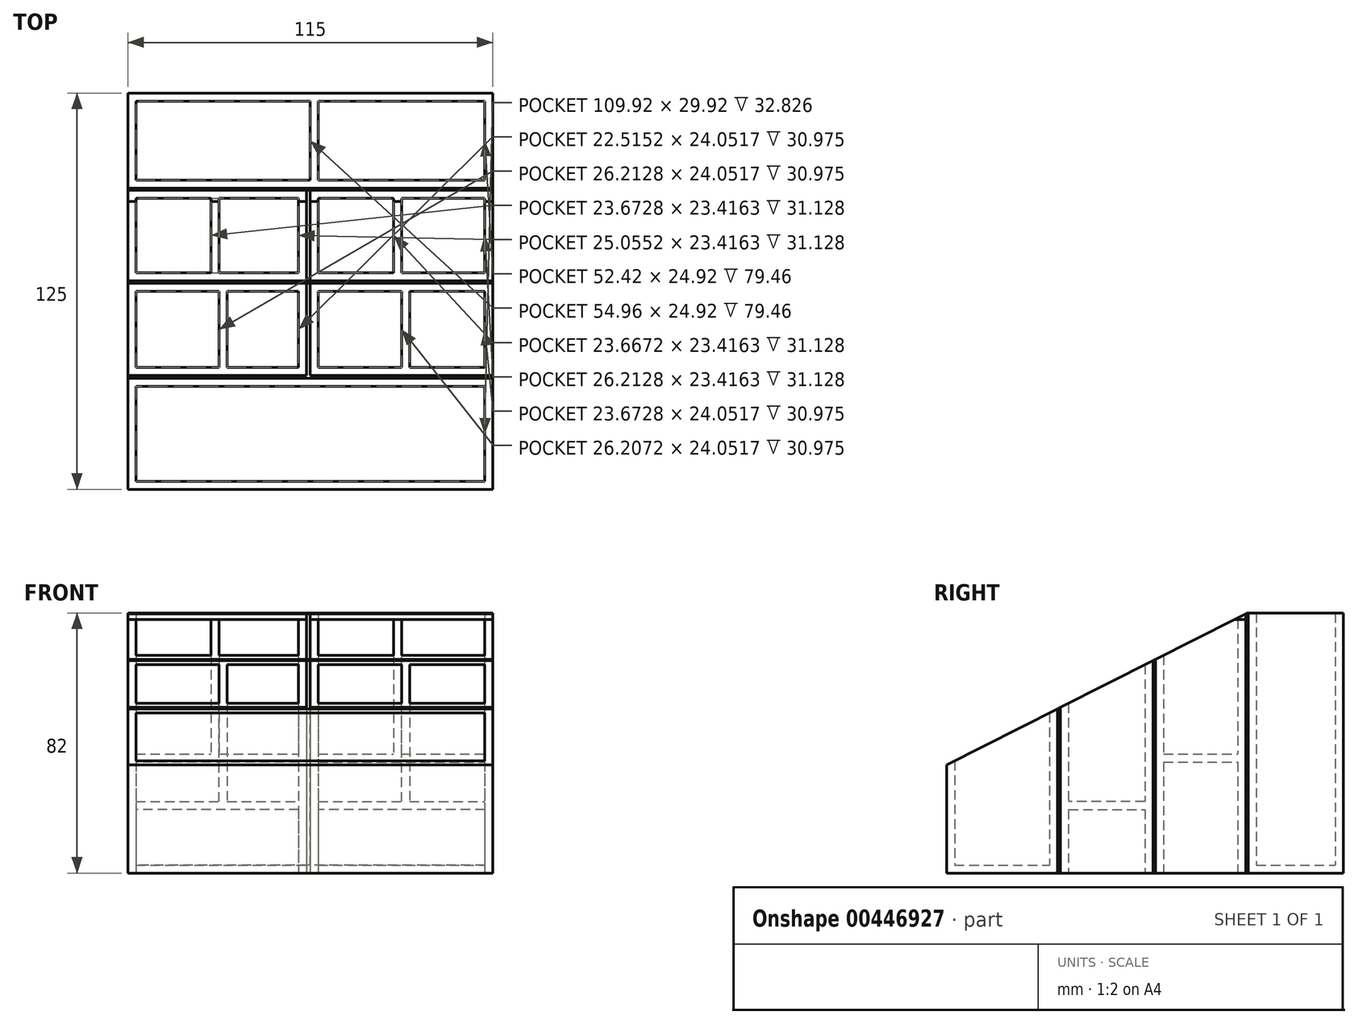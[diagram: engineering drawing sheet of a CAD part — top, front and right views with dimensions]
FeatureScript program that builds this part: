
annotation { "Feature Type Name" : "Feature", "Feature Type Description" : "" }
export const myFeature = defineFeature(function(context is Context, id is Id, definition is map)
    precondition{}
    {
        {
            var Q0;
            Q0=qCreatedBy(makeId("Top.planeOp"),FACE);
            var sketch = newSketch(context, id + "F0", { "sketchPlane" : qUnion([Q0])});
            skLineSegment(sketch, "E0.bottom", {"start": v(57.5, -62.5) * mm, "end": v(-57.5, -62.5) * mm});
            skLineSegment(sketch, "E0.top", {"start": v(57.5, 62.5) * mm, "end": v(-57.5, 62.5) * mm});
            skLineSegment(sketch, "E0.left", {"start": v(57.5, -62.5) * mm, "end": v(57.5, 62.5) * mm});
            skLineSegment(sketch, "E0.right", {"start": v(-57.5, -62.5) * mm, "end": v(-57.5, 62.5) * mm});
            skPoint(sketch, "E0.middle", {"position": v(0, 0) * mm});
            skLineSegment(sketch, "E1", {"start": v(0, 62.5) * mm, "end": v(0, -27.5) * mm});
            skLineSegment(sketch, "E2", {"start": v(0, -27.5) * mm, "end": v(57.5, -27.5) * mm});
            skLineSegment(sketch, "E3", {"start": v(0, -27.5) * mm, "end": v(-57.5, -27.5) * mm});
            skLineSegment(sketch, "E4", {"start": v(-57.5, 32.5) * mm, "end": v(57.5, 32.5) * mm});
            skLineSegment(sketch, "E5", {"start": v(-57.5, 2.5) * mm, "end": v(57.5, 2.5) * mm});
            skLineSegment(sketch, "E6", {"start": v(28.75, 32.5) * mm, "end": v(28.75, -27.5) * mm});
            skLineSegment(sketch, "E7", {"start": v(-28.75, 32.5) * mm, "end": v(-28.75, -27.5) * mm});
            skLineSegment(sketch, "E8", {"start": v(-57.5, -26.63) * mm, "end": v(-28.75, -26.63) * mm});
            skLineSegment(sketch, "E9", {"start": v(-28.75, -26.63) * mm, "end": v(0, -26.63) * mm});
            skLineSegment(sketch, "E10", {"start": v(0, -26.63) * mm, "end": v(28.75, -26.63) * mm});
            skLineSegment(sketch, "E11", {"start": v(28.75, -26.63) * mm, "end": v(57.5, -26.63) * mm});
            skLineSegment(sketch, "E12", {"start": v(-1.15, -26.63) * mm, "end": v(-1.15, 2.5) * mm});
            skLineSegment(sketch, "E13", {"start": v(-1.15, 2.5) * mm, "end": v(-1.15, 32.5) * mm});
            skPoint(sketch, "E13.endSnap0", {"position": v(0, 32.5) * mm});
            skLineSegment(sketch, "E14", {"start": v(-57.5, 3.32) * mm, "end": v(-28.75, 3.32) * mm});
            skLineSegment(sketch, "E15", {"start": v(-28.75, 3.32) * mm, "end": v(0, 3.32) * mm});
            skLineSegment(sketch, "E16", {"start": v(0, 3.32) * mm, "end": v(28.75, 3.32) * mm});
            skLineSegment(sketch, "E17", {"start": v(28.75, 3.32) * mm, "end": v(57.5, 3.32) * mm});
            skLineSegment(sketch, "E18", {"start": v(-57.5, 31.81) * mm, "end": v(-28.75, 31.81) * mm});
            skLineSegment(sketch, "E19", {"start": v(-28.75, 31.81) * mm, "end": v(0, 31.81) * mm});
            skLineSegment(sketch, "E20", {"start": v(0, 31.81) * mm, "end": v(28.75, 31.81) * mm});
            skLineSegment(sketch, "E21", {"start": v(28.75, 31.81) * mm, "end": v(57.5, 31.81) * mm});
            skSolve(sketch);
        }
        {
            var Q0;
            {var subQ4=sQuery(id+"F0.wireOp",EDGE,"E0.top");var subQ6=sQuery(id+"F0.wireOp",EDGE,"E0.left");var subQ7=makeQuery(id+"F0.imprint","INTERSECT",VERTEX,{"derivedFrom":[subQ4,subQ6]});Q0=makeQuery(id+"F0.imprint","IMPRINT",FACE,{"disambiguationData":[TD([[makeQuery(id+"F0.imprint","IMPRINT",EDGE,{"disambiguationData":[TD([[subQ7,-1.0]])],"derivedFrom":subQ4}),1.0]])]});}
            extrude(context, id + "F1", {"entities" : qUnion([Q0]), "depth" : 82 * mm});
        }
        {
            var Q0;
            Q0=makeQuery(id+"F1.opExtrude","CAP_FACE",FACE,{"disambiguationData":[OSD([sQuery(id+"F0.wireOp",EDGE,"E0.top"),sQuery(id+"F0.wireOp",EDGE,"E0.left"),sQuery(id+"F0.wireOp",EDGE,"E1"),sQuery(id+"F0.wireOp",EDGE,"E4")])],"isStart":false});
            shell(context, id + "F2", {"entities" : qUnion([Q0]), "thickness" : 2.54 * mm});
        }
        {
            var Q0;
            {var subQ1=sQuery(id+"F0.wireOp",EDGE,"E0.right");var subQ5=sQuery(id+"F0.wireOp",EDGE,"E0.top");var subQ8=makeQuery(id+"F0.imprint","INTERSECT",VERTEX,{"derivedFrom":[subQ5,subQ1]});Q0=makeQuery(id+"F0.imprint","IMPRINT",FACE,{"disambiguationData":[TD([[makeQuery(id+"F0.imprint","IMPRINT",EDGE,{"disambiguationData":[TD([[subQ8,1.0]])],"derivedFrom":subQ5}),1.0]])]});}
            extrude(context, id + "F3", {"entities" : qUnion([Q0]), "operationType" : NewBodyOperationType.ADD, "depth" : 82 * mm});
        }
        {
            var Q0;
            {var subQ0=sQuery(id+"F0.wireOp",EDGE,"E4");var subQ1=sQuery(id+"F0.wireOp",EDGE,"E1");var subQ2=sQuery(id+"F0.wireOp",EDGE,"E0.top");Q0=makeQuery(id+"F3.boolean.opBoolean","MERGE",FACE,{"derivedFrom":[makeQuery(id+"F1.opExtrude","CAP_FACE",FACE,{"disambiguationData":[OSD([subQ2,sQuery(id+"F0.wireOp",EDGE,"E0.left"),subQ1,subQ0])],"isStart":false}),makeQuery(id+"F3.opExtrude","CAP_FACE",FACE,{"disambiguationData":[OSD([subQ2,sQuery(id+"F0.wireOp",EDGE,"E0.right"),subQ1,subQ0])],"isStart":false})]});}
            shell(context, id + "F4", {"entities" : qUnion([Q0]), "thickness" : 2.54 * mm});
        }
        {
            var Q0;
            {var subQ5=sQuery(id+"F0.wireOp",EDGE,"E0.bottom");Q0=makeQuery(id+"F0.imprint","IMPRINT",FACE,{"disambiguationData":[TD([[makeQuery(id+"F0.imprint","IMPRINT",EDGE,{"derivedFrom":subQ5}),-1.0]])]});}
            extrude(context, id + "F5", {"entities" : qUnion([Q0]), "depth" : 52 * mm});
        }
        {
            var Q0;
            Q0=makeQuery(id+"F5.opExtrude","CAP_FACE",FACE,{"disambiguationData":[OSD([sQuery(id+"F0.wireOp",EDGE,"E0.bottom"),sQuery(id+"F0.wireOp",EDGE,"E0.left"),sQuery(id+"F0.wireOp",EDGE,"E0.right"),sQuery(id+"F0.wireOp",EDGE,"E2"),sQuery(id+"F0.wireOp",EDGE,"E3")])],"isStart":false});
            shell(context, id + "F6", {"entities" : qUnion([Q0]), "thickness" : 2.54 * mm});
        }
        {
            var Q0;
            {var subQ3=sQuery(id+"F0.wireOp",EDGE,"E11");Q0=makeQuery(id+"F0.imprint","IMPRINT",FACE,{"disambiguationData":[TD([[makeQuery(id+"F0.imprint","IMPRINT",EDGE,{"derivedFrom":subQ3}),1.0]])]});}
            extrude(context, id + "F7", {"entities" : qUnion([Q0]), "depth" : 70 * mm});
        }
        {
            var Q0;
            Q0=makeQuery(id+"F7.opExtrude","CAP_FACE",FACE,{"disambiguationData":[OSD([sQuery(id+"F0.wireOp",EDGE,"E0.left"),sQuery(id+"F0.wireOp",EDGE,"E5"),sQuery(id+"F0.wireOp",EDGE,"E6"),sQuery(id+"F0.wireOp",EDGE,"E11")])],"isStart":false});
            shell(context, id + "F8", {"entities" : qUnion([Q0]), "thickness" : 2.54 * mm});
        }
        {
            var Q0;
            Q0=makeQuery(id+"F8.opShell","OFFSET_FACE",FACE,{"disambiguationData":[OSD([sQuery(id+"F0.wireOp",EDGE,"E0.left"),sQuery(id+"F0.wireOp",EDGE,"E5"),sQuery(id+"F0.wireOp",EDGE,"E6"),sQuery(id+"F0.wireOp",EDGE,"E11")])]});
            extrude(context, id + "F9", {"entities" : qUnion([Q0]), "operationType" : NewBodyOperationType.ADD, "depth" : 20 * mm});
        }
        {
            var Q0;
            {var subQ0=sQuery(id+"F0.wireOp",EDGE,"E10");Q0=makeQuery(id+"F0.imprint","IMPRINT",FACE,{"disambiguationData":[TD([[makeQuery(id+"F0.imprint","IMPRINT",EDGE,{"derivedFrom":subQ0}),1.0]])]});}
            extrude(context, id + "F10", {"entities" : qUnion([Q0]), "operationType" : NewBodyOperationType.ADD, "depth" : 70 * mm});
        }
        {
            var Q0;
            {var subQ0=sQuery(id+"F0.wireOp",EDGE,"E6");var subQ1=sQuery(id+"F0.wireOp",EDGE,"E5");Q0=makeQuery(id+"F10.boolean.opBoolean","MERGE",FACE,{"derivedFrom":[makeQuery(id+"F7.opExtrude","CAP_FACE",FACE,{"disambiguationData":[OSD([sQuery(id+"F0.wireOp",EDGE,"E0.left"),subQ1,subQ0,sQuery(id+"F0.wireOp",EDGE,"E11")])],"isStart":false}),makeQuery(id+"F10.opExtrude","CAP_FACE",FACE,{"disambiguationData":[OSD([sQuery(id+"F0.wireOp",EDGE,"E1"),subQ1,subQ0,sQuery(id+"F0.wireOp",EDGE,"E10")])],"isStart":false})]});}
            shell(context, id + "F11", {"entities" : qUnion([Q0]), "thickness" : 2.54 * mm});
        }
        {
            var Q0;
            Q0=makeQuery(id+"F11.opShell","OFFSET_FACE",FACE,{"disambiguationData":[OSD([sQuery(id+"F0.wireOp",EDGE,"E0.left"),sQuery(id+"F0.wireOp",EDGE,"E1"),sQuery(id+"F0.wireOp",EDGE,"E5"),sQuery(id+"F0.wireOp",EDGE,"E6"),sQuery(id+"F0.wireOp",EDGE,"E10"),sQuery(id+"F0.wireOp",EDGE,"E11")])]});
            extrude(context, id + "F12", {"entities" : qUnion([Q0]), "operationType" : NewBodyOperationType.ADD, "depth" : 20 * mm});
        }
        {
            var Q0;
            {var subQ0=sQuery(id+"F0.wireOp",EDGE,"E6");var subQ1=sQuery(id+"F0.wireOp",EDGE,"E5");Q0=makeQuery(id+"F10.boolean.opBoolean","MERGE",FACE,{"derivedFrom":[makeQuery(id+"F7.opExtrude","CAP_FACE",FACE,{"disambiguationData":[OSD([sQuery(id+"F0.wireOp",EDGE,"E0.left"),subQ1,subQ0,sQuery(id+"F0.wireOp",EDGE,"E11")])],"isStart":true}),makeQuery(id+"F10.opExtrude","CAP_FACE",FACE,{"disambiguationData":[OSD([sQuery(id+"F0.wireOp",EDGE,"E1"),subQ1,subQ0,sQuery(id+"F0.wireOp",EDGE,"E10")])],"isStart":true})]});}
            shell(context, id + "F13", {"entities" : qUnion([Q0]), "thickness" : 2.54 * mm});
        }
        {
            var Q0;
            {var subQ0=sQuery(id+"F0.wireOp",EDGE,"E12");Q0=makeQuery(id+"F0.imprint","IMPRINT",FACE,{"disambiguationData":[TD([[makeQuery(id+"F0.imprint","IMPRINT",EDGE,{"derivedFrom":subQ0}),1.0]])]});}
            extrude(context, id + "F14", {"entities" : qUnion([Q0]), "depth" : 70 * mm});
        }
        {
            var Q0;
            Q0=makeQuery(id+"F14.opExtrude","CAP_FACE",FACE,{"disambiguationData":[OSD([sQuery(id+"F0.wireOp",EDGE,"E5"),sQuery(id+"F0.wireOp",EDGE,"E7"),sQuery(id+"F0.wireOp",EDGE,"E9"),sQuery(id+"F0.wireOp",EDGE,"E12")])],"isStart":false});
            shell(context, id + "F15", {"entities" : qUnion([Q0]), "thickness" : 2.54 * mm});
        }
        {
            var Q0;
            Q0=makeQuery(id+"F15.opShell","OFFSET_FACE",FACE,{"disambiguationData":[OSD([sQuery(id+"F0.wireOp",EDGE,"E5"),sQuery(id+"F0.wireOp",EDGE,"E7"),sQuery(id+"F0.wireOp",EDGE,"E9"),sQuery(id+"F0.wireOp",EDGE,"E12")])]});
            extrude(context, id + "F16", {"entities" : qUnion([Q0]), "operationType" : NewBodyOperationType.ADD, "depth" : 20 * mm});
        }
        {
            var Q0;
            {var subQ3=sQuery(id+"F0.wireOp",EDGE,"E8");Q0=makeQuery(id+"F0.imprint","IMPRINT",FACE,{"disambiguationData":[TD([[makeQuery(id+"F0.imprint","IMPRINT",EDGE,{"derivedFrom":subQ3}),1.0]])]});}
            extrude(context, id + "F17", {"entities" : qUnion([Q0]), "operationType" : NewBodyOperationType.ADD, "depth" : 70 * mm});
        }
        {
            var Q0;
            {var subQ0=sQuery(id+"F0.wireOp",EDGE,"E7");var subQ1=sQuery(id+"F0.wireOp",EDGE,"E5");Q0=makeQuery(id+"F17.boolean.opBoolean","MERGE",FACE,{"derivedFrom":[makeQuery(id+"F14.opExtrude","CAP_FACE",FACE,{"disambiguationData":[OSD([subQ1,subQ0,sQuery(id+"F0.wireOp",EDGE,"E9"),sQuery(id+"F0.wireOp",EDGE,"E12")])],"isStart":false}),makeQuery(id+"F17.opExtrude","CAP_FACE",FACE,{"disambiguationData":[OSD([sQuery(id+"F0.wireOp",EDGE,"E0.right"),subQ1,subQ0,sQuery(id+"F0.wireOp",EDGE,"E8")])],"isStart":false})]});}
            shell(context, id + "F18", {"entities" : qUnion([Q0]), "thickness" : 2.54 * mm});
        }
        {
            var Q0;
            Q0=makeQuery(id+"F18.opShell","OFFSET_FACE",FACE,{"disambiguationData":[OSD([sQuery(id+"F0.wireOp",EDGE,"E0.right"),sQuery(id+"F0.wireOp",EDGE,"E5"),sQuery(id+"F0.wireOp",EDGE,"E7"),sQuery(id+"F0.wireOp",EDGE,"E8"),sQuery(id+"F0.wireOp",EDGE,"E9"),sQuery(id+"F0.wireOp",EDGE,"E12")])]});
            extrude(context, id + "F19", {"entities" : qUnion([Q0]), "operationType" : NewBodyOperationType.ADD, "depth" : 20 * mm});
        }
        {
            var Q0;
            {var subQ0=sQuery(id+"F0.wireOp",EDGE,"E7");var subQ1=sQuery(id+"F0.wireOp",EDGE,"E5");Q0=makeQuery(id+"F17.boolean.opBoolean","MERGE",FACE,{"derivedFrom":[makeQuery(id+"F14.opExtrude","CAP_FACE",FACE,{"disambiguationData":[OSD([subQ1,subQ0,sQuery(id+"F0.wireOp",EDGE,"E9"),sQuery(id+"F0.wireOp",EDGE,"E12")])],"isStart":true}),makeQuery(id+"F17.opExtrude","CAP_FACE",FACE,{"disambiguationData":[OSD([sQuery(id+"F0.wireOp",EDGE,"E0.right"),subQ1,subQ0,sQuery(id+"F0.wireOp",EDGE,"E8")])],"isStart":true})]});}
            shell(context, id + "F20", {"entities" : qUnion([Q0]), "thickness" : 2.54 * mm});
        }
        {
            var Q0;
            {var subQ0=sQuery(id+"F0.wireOp",EDGE,"E14");Q0=makeQuery(id+"F0.imprint","IMPRINT",FACE,{"disambiguationData":[TD([[makeQuery(id+"F0.imprint","IMPRINT",EDGE,{"derivedFrom":subQ0}),1.0]])]});}
            extrude(context, id + "F21", {"entities" : qUnion([Q0]), "depth" : 80 * mm});
        }
        {
            var Q0;
            Q0=makeQuery(id+"F21.opExtrude","CAP_FACE",FACE,{"disambiguationData":[OSD([sQuery(id+"F0.wireOp",EDGE,"E0.right"),sQuery(id+"F0.wireOp",EDGE,"E7"),sQuery(id+"F0.wireOp",EDGE,"E14"),sQuery(id+"F0.wireOp",EDGE,"E18")])],"isStart":false});
            shell(context, id + "F22", {"entities" : qUnion([Q0]), "thickness" : 2.54 * mm});
        }
        {
            var Q0;
            Q0=makeQuery(id+"F22.opShell","OFFSET_FACE",FACE,{"disambiguationData":[OSD([sQuery(id+"F0.wireOp",EDGE,"E0.right"),sQuery(id+"F0.wireOp",EDGE,"E7"),sQuery(id+"F0.wireOp",EDGE,"E14"),sQuery(id+"F0.wireOp",EDGE,"E18")])]});
            extrude(context, id + "F23", {"entities" : qUnion([Q0]), "operationType" : NewBodyOperationType.ADD, "depth" : 35 * mm});
        }
        {
            var Q0;
            {var subQ0=sQuery(id+"F0.wireOp",EDGE,"E15");var subQ5=sQuery(id+"F0.wireOp",EDGE,"E13");var subQ6=makeQuery(id+"F0.imprint","INTERSECT",VERTEX,{"derivedFrom":[subQ5,subQ0]});Q0=makeQuery(id+"F0.imprint","IMPRINT",FACE,{"disambiguationData":[TD([[makeQuery(id+"F0.imprint","IMPRINT",EDGE,{"disambiguationData":[TD([[subQ6,-1.0]])],"derivedFrom":subQ5}),1.0]])]});}
            extrude(context, id + "F24", {"entities" : qUnion([Q0]), "operationType" : NewBodyOperationType.ADD, "depth" : 80 * mm});
        }
        {
            var Q0;
            {var subQ0=sQuery(id+"F0.wireOp",EDGE,"E7");Q0=makeQuery(id+"F24.boolean.opBoolean","MERGE",FACE,{"derivedFrom":[makeQuery(id+"F21.opExtrude","CAP_FACE",FACE,{"disambiguationData":[OSD([sQuery(id+"F0.wireOp",EDGE,"E0.right"),subQ0,sQuery(id+"F0.wireOp",EDGE,"E14"),sQuery(id+"F0.wireOp",EDGE,"E18")])],"isStart":false}),makeQuery(id+"F24.opExtrude","CAP_FACE",FACE,{"disambiguationData":[OSD([subQ0,sQuery(id+"F0.wireOp",EDGE,"E13"),sQuery(id+"F0.wireOp",EDGE,"E15"),sQuery(id+"F0.wireOp",EDGE,"E19")])],"isStart":false})]});}
            shell(context, id + "F25", {"entities" : qUnion([Q0]), "thickness" : 2.54 * mm});
        }
        {
            var Q0;
            Q0=makeQuery(id+"F25.opShell","OFFSET_FACE",FACE,{"disambiguationData":[OSD([sQuery(id+"F0.wireOp",EDGE,"E0.right"),sQuery(id+"F0.wireOp",EDGE,"E7"),sQuery(id+"F0.wireOp",EDGE,"E13"),sQuery(id+"F0.wireOp",EDGE,"E14"),sQuery(id+"F0.wireOp",EDGE,"E15"),sQuery(id+"F0.wireOp",EDGE,"E18"),sQuery(id+"F0.wireOp",EDGE,"E19")])]});
            extrude(context, id + "F26", {"entities" : qUnion([Q0]), "operationType" : NewBodyOperationType.ADD, "depth" : 35 * mm});
        }
        {
            var Q0;
            {var subQ0=sQuery(id+"F0.wireOp",EDGE,"E16");Q0=makeQuery(id+"F0.imprint","IMPRINT",FACE,{"disambiguationData":[TD([[makeQuery(id+"F0.imprint","IMPRINT",EDGE,{"derivedFrom":subQ0}),1.0]])]});}
            extrude(context, id + "F27", {"entities" : qUnion([Q0]), "depth" : 80 * mm});
        }
        {
            var Q0;
            Q0=makeQuery(id+"F27.opExtrude","CAP_FACE",FACE,{"disambiguationData":[OSD([sQuery(id+"F0.wireOp",EDGE,"E1"),sQuery(id+"F0.wireOp",EDGE,"E6"),sQuery(id+"F0.wireOp",EDGE,"E16"),sQuery(id+"F0.wireOp",EDGE,"E20")])],"isStart":false});
            shell(context, id + "F28", {"entities" : qUnion([Q0]), "thickness" : 2.54 * mm});
        }
        {
            var Q0;
            Q0=makeQuery(id+"F28.opShell","OFFSET_FACE",FACE,{"disambiguationData":[OSD([sQuery(id+"F0.wireOp",EDGE,"E1"),sQuery(id+"F0.wireOp",EDGE,"E6"),sQuery(id+"F0.wireOp",EDGE,"E16"),sQuery(id+"F0.wireOp",EDGE,"E20")])]});
            extrude(context, id + "F29", {"entities" : qUnion([Q0]), "operationType" : NewBodyOperationType.ADD, "depth" : 35 * mm});
        }
        {
            var Q0;
            {var subQ0=sQuery(id+"F0.wireOp",EDGE,"E17");Q0=makeQuery(id+"F0.imprint","IMPRINT",FACE,{"disambiguationData":[TD([[makeQuery(id+"F0.imprint","IMPRINT",EDGE,{"derivedFrom":subQ0}),1.0]])]});}
            extrude(context, id + "F30", {"entities" : qUnion([Q0]), "operationType" : NewBodyOperationType.ADD, "depth" : 80 * mm});
        }
        {
            var Q0;
            {var subQ0=sQuery(id+"F0.wireOp",EDGE,"E6");Q0=makeQuery(id+"F30.boolean.opBoolean","MERGE",FACE,{"derivedFrom":[makeQuery(id+"F27.opExtrude","CAP_FACE",FACE,{"disambiguationData":[OSD([sQuery(id+"F0.wireOp",EDGE,"E1"),subQ0,sQuery(id+"F0.wireOp",EDGE,"E16"),sQuery(id+"F0.wireOp",EDGE,"E20")])],"isStart":false}),makeQuery(id+"F30.opExtrude","CAP_FACE",FACE,{"disambiguationData":[OSD([sQuery(id+"F0.wireOp",EDGE,"E0.left"),subQ0,sQuery(id+"F0.wireOp",EDGE,"E17"),sQuery(id+"F0.wireOp",EDGE,"E21")])],"isStart":false})]});}
            shell(context, id + "F31", {"entities" : qUnion([Q0]), "thickness" : 2.54 * mm});
        }
        {
            var Q0;
            Q0=makeQuery(id+"F31.opShell","OFFSET_FACE",FACE,{"disambiguationData":[OSD([sQuery(id+"F0.wireOp",EDGE,"E0.left"),sQuery(id+"F0.wireOp",EDGE,"E1"),sQuery(id+"F0.wireOp",EDGE,"E6"),sQuery(id+"F0.wireOp",EDGE,"E16"),sQuery(id+"F0.wireOp",EDGE,"E17"),sQuery(id+"F0.wireOp",EDGE,"E20"),sQuery(id+"F0.wireOp",EDGE,"E21")])]});
            extrude(context, id + "F32", {"entities" : qUnion([Q0]), "operationType" : NewBodyOperationType.ADD, "depth" : 35 * mm});
        }
        {
            var Q0;
            {var subQ0=sQuery(id+"F0.wireOp",EDGE,"E6");Q0=makeQuery(id+"F30.boolean.opBoolean","MERGE",FACE,{"derivedFrom":[makeQuery(id+"F27.opExtrude","CAP_FACE",FACE,{"disambiguationData":[OSD([sQuery(id+"F0.wireOp",EDGE,"E1"),subQ0,sQuery(id+"F0.wireOp",EDGE,"E16"),sQuery(id+"F0.wireOp",EDGE,"E20")])],"isStart":true}),makeQuery(id+"F30.opExtrude","CAP_FACE",FACE,{"disambiguationData":[OSD([sQuery(id+"F0.wireOp",EDGE,"E0.left"),subQ0,sQuery(id+"F0.wireOp",EDGE,"E17"),sQuery(id+"F0.wireOp",EDGE,"E21")])],"isStart":true})]});}
            var Q1;
            {var subQ0=sQuery(id+"F0.wireOp",EDGE,"E7");Q1=makeQuery(id+"F24.boolean.opBoolean","MERGE",FACE,{"derivedFrom":[makeQuery(id+"F21.opExtrude","CAP_FACE",FACE,{"disambiguationData":[OSD([sQuery(id+"F0.wireOp",EDGE,"E0.right"),subQ0,sQuery(id+"F0.wireOp",EDGE,"E14"),sQuery(id+"F0.wireOp",EDGE,"E18")])],"isStart":true}),makeQuery(id+"F24.opExtrude","CAP_FACE",FACE,{"disambiguationData":[OSD([subQ0,sQuery(id+"F0.wireOp",EDGE,"E13"),sQuery(id+"F0.wireOp",EDGE,"E15"),sQuery(id+"F0.wireOp",EDGE,"E19")])],"isStart":true})]});}
            shell(context, id + "F33", {"entities" : qUnion([Q0, Q1]), "thickness" : 2.54 * mm});
        }
        {
            var Q0;
            {var subQ1=sQuery(id+"F0.wireOp",EDGE,"E7");var subQ4=sQuery(id+"F0.wireOp",EDGE,"E3");var subQ5=makeQuery(id+"F0.imprint","INTERSECT",VERTEX,{"derivedFrom":[subQ4,subQ1]});Q0=makeQuery(id+"F0.imprint","IMPRINT",FACE,{"disambiguationData":[TD([[makeQuery(id+"F0.imprint","IMPRINT",EDGE,{"disambiguationData":[TD([[subQ5,1.0]])],"derivedFrom":subQ4}),-1.0]])]});}
            var Q1;
            {var subQ3=sQuery(id+"F0.wireOp",EDGE,"E8");Q1=makeQuery(id+"F0.imprint","IMPRINT",FACE,{"disambiguationData":[TD([[makeQuery(id+"F0.imprint","IMPRINT",EDGE,{"derivedFrom":subQ3}),-1.0]])]});}
            var Q2;
            {var subQ3=sQuery(id+"F0.wireOp",EDGE,"E11");Q2=makeQuery(id+"F0.imprint","IMPRINT",FACE,{"disambiguationData":[TD([[makeQuery(id+"F0.imprint","IMPRINT",EDGE,{"derivedFrom":subQ3}),-1.0]])]});}
            var Q3;
            {var subQ3=sQuery(id+"F0.wireOp",EDGE,"E10");Q3=makeQuery(id+"F0.imprint","IMPRINT",FACE,{"disambiguationData":[TD([[makeQuery(id+"F0.imprint","IMPRINT",EDGE,{"derivedFrom":subQ3}),-1.0]])]});}
            var Q4;
            {var subQ5=sQuery(id+"F0.wireOp",EDGE,"E12");Q4=makeQuery(id+"F0.imprint","IMPRINT",FACE,{"disambiguationData":[TD([[makeQuery(id+"F0.imprint","IMPRINT",EDGE,{"derivedFrom":subQ5}),-1.0]])]});}
            var Q5;
            {var subQ0=sQuery(id+"F0.wireOp",EDGE,"E16");Q5=makeQuery(id+"F0.imprint","IMPRINT",FACE,{"disambiguationData":[TD([[makeQuery(id+"F0.imprint","IMPRINT",EDGE,{"derivedFrom":subQ0}),-1.0]])]});}
            var Q6;
            {var subQ3=sQuery(id+"F0.wireOp",EDGE,"E17");Q6=makeQuery(id+"F0.imprint","IMPRINT",FACE,{"disambiguationData":[TD([[makeQuery(id+"F0.imprint","IMPRINT",EDGE,{"derivedFrom":subQ3}),-1.0]])]});}
            var Q7;
            {var subQ1=sQuery(id+"F0.wireOp",EDGE,"E5");var subQ3=sQuery(id+"F0.wireOp",EDGE,"E7");var subQ4=makeQuery(id+"F0.imprint","INTERSECT",VERTEX,{"derivedFrom":[subQ1,subQ3]});Q7=makeQuery(id+"F0.imprint","IMPRINT",FACE,{"disambiguationData":[TD([[makeQuery(id+"F0.imprint","IMPRINT",EDGE,{"disambiguationData":[TD([[subQ4,-1.0]])],"derivedFrom":subQ1}),1.0]])]});}
            var Q8;
            {var subQ3=sQuery(id+"F0.wireOp",EDGE,"E14");Q8=makeQuery(id+"F0.imprint","IMPRINT",FACE,{"disambiguationData":[TD([[makeQuery(id+"F0.imprint","IMPRINT",EDGE,{"derivedFrom":subQ3}),-1.0]])]});}
            var Q9;
            {var subQ3=sQuery(id+"F0.wireOp",EDGE,"E18");Q9=makeQuery(id+"F0.imprint","IMPRINT",FACE,{"disambiguationData":[TD([[makeQuery(id+"F0.imprint","IMPRINT",EDGE,{"derivedFrom":subQ3}),1.0]])]});}
            var Q10;
            {var subQ0=sQuery(id+"F0.wireOp",EDGE,"E7");var subQ1=sQuery(id+"F0.wireOp",EDGE,"E4");var subQ2=makeQuery(id+"F0.imprint","INTERSECT",VERTEX,{"derivedFrom":[subQ1,subQ0]});Q10=makeQuery(id+"F0.imprint","IMPRINT",FACE,{"disambiguationData":[TD([[makeQuery(id+"F0.imprint","IMPRINT",EDGE,{"disambiguationData":[TD([[subQ2,-1.0]])],"derivedFrom":subQ1}),-1.0]])]});}
            var Q11;
            {var subQ0=sQuery(id+"F0.wireOp",EDGE,"E15");var subQ5=sQuery(id+"F0.wireOp",EDGE,"E13");var subQ6=makeQuery(id+"F0.imprint","INTERSECT",VERTEX,{"derivedFrom":[subQ5,subQ0]});Q11=makeQuery(id+"F0.imprint","IMPRINT",FACE,{"disambiguationData":[TD([[makeQuery(id+"F0.imprint","IMPRINT",EDGE,{"disambiguationData":[TD([[subQ6,-1.0]])],"derivedFrom":subQ5}),-1.0]])]});}
            var Q12;
            {var subQ0=sQuery(id+"F0.wireOp",EDGE,"E20");Q12=makeQuery(id+"F0.imprint","IMPRINT",FACE,{"disambiguationData":[TD([[makeQuery(id+"F0.imprint","IMPRINT",EDGE,{"derivedFrom":subQ0}),1.0]])]});}
            var Q13;
            {var subQ3=sQuery(id+"F0.wireOp",EDGE,"E21");Q13=makeQuery(id+"F0.imprint","IMPRINT",FACE,{"disambiguationData":[TD([[makeQuery(id+"F0.imprint","IMPRINT",EDGE,{"derivedFrom":subQ3}),1.0]])]});}
            extrude(context, id + "F34", {"entities" : qUnion([Q0, Q1, Q2, Q3, Q4, Q5, Q6, Q7, Q8, Q9, Q10, Q11, Q12, Q13]), "depth" : 82 * mm});
        }
        {
            var Q0;
            Q0=qCreatedBy(makeId("Right.planeOp"),FACE);
            var sketch = newSketch(context, id + "F35", { "sketchPlane" : qUnion([Q0])});
            skLineSegment(sketch, "E22", {"start": v(32.77, 82.28) * mm, "end": v(-62.77, 33.95) * mm});
            skLineSegment(sketch, "E23", {"start": v(-62.77, 33.95) * mm, "end": v(-62.77, 108.73) * mm});
            skLineSegment(sketch, "E24", {"start": v(-62.77, 108.73) * mm, "end": v(33.6, 108.73) * mm});
            skLineSegment(sketch, "E25", {"start": v(33.6, 108.73) * mm, "end": v(32.77, 82.28) * mm});
            skSolve(sketch);
        }
        {
            var Q0;
            Q0 = qSketchRegion(id + "F35", true);
            extrude(context, id + "F36", {"entities" : qUnion([Q0]), "operationType" : NewBodyOperationType.REMOVE, "endBound" : BoundingType.SYMMETRIC, "depth" : 225.55 * mm});
        }
    });
